# Revit family: 873-00-001-DN450-600
name_source: partatom
category: Pipe Accessories
units: mm (PartAtom-declared; Revit-internal decimal feet)

## family parameters
Always vertical = Yes
Cut with Voids When Loaded = No
Part Type = Valve - Breaks Into
Round Connector Dimension = Use Diameter
Shared = No
Work Plane-Based = No

## types (6) — shared parameters
873-0450-00-041000 = DN450_PN10
873-0450-00-141000 = DN450_PN16
873-0500-00-041000 = DN500_PN10
873-0500-00-141000 = DN500_PN16
873-0600-00-041000 = DN600_PN10
873-0600-00-141000 = DN600_PN16
Angle = 22.50°
Body_Wallthicknss = 10 mm  [stored 0.0328084 ft]
Description_ = AVK DISMANTLING JOINT
Flange_thickness = 20 mm  [stored 0.0656168 ft]
Search_table = 873-00-001-DN450-600
URL product pages = https://www.avkvalves.com

## per-type parameters (varying)
| type | A | DN | Id(Radius) | L | T | d1 | d2 |
| DN450_PN10 | 270 mm  [stored 0.885827 ft] | 450 mm  [stored 1.47638 ft] | 225 mm  [stored 0.738189 ft] | 435 mm  [stored 1.42717 ft] | 24 mm  [stored 0.0787402 ft] | 565 mm  [stored 1.85367 ft] | 308 mm |
| DN450_PN16 | 270 mm  [stored 0.885827 ft] | 450 mm  [stored 1.47638 ft] | 225 mm  [stored 0.738189 ft] | 450 mm  [stored 1.47638 ft] | 27 mm  [stored 0.0885827 ft] | 585 mm  [stored 1.91929 ft] | 320 mm  [stored 1.04987 ft] |
| DN500_PN10 | 270 mm  [stored 0.885827 ft] | 500 mm  [stored 1.64042 ft] | 250 mm  [stored 0.82021 ft] | 440 mm  [stored 1.44357 ft] | 24 mm  [stored 0.0787402 ft] | 620 mm  [stored 2.03412 ft] | 335 mm  [stored 1.09908 ft] |
| DN500_PN16 | 270 mm  [stored 0.885827 ft] | 500 mm  [stored 1.64042 ft] | 250 mm  [stored 0.82021 ft] | 460 mm  [stored 1.50919 ft] | 30 mm  [stored 0.0984252 ft] | 650 mm  [stored 2.13255 ft] | 358 mm |
| DN600_PN10 | 290 mm  [stored 0.951444 ft] | 600 mm  [stored 1.9685 ft] | 300 mm | 460 mm  [stored 1.50919 ft] | 27 mm  [stored 0.0885827 ft] | 725 mm  [stored 2.37861 ft] | 390 mm  [stored 1.27953 ft] |
| DN600_PN16 | 290 mm  [stored 0.951444 ft] | 600 mm  [stored 1.9685 ft] | 300 mm | 500 mm  [stored 1.64042 ft] | 33 mm  [stored 0.108268 ft] | 770 mm  [stored 2.52625 ft] | 420 mm  [stored 1.37795 ft] |

note: [stored X ft] marks values corroborated as IEEE doubles in the binary element streams (Revit-internal decimal feet)

## geometry (parser evidence)
native form markers: Sweep x5
no freeform markers — native parametric forms only
